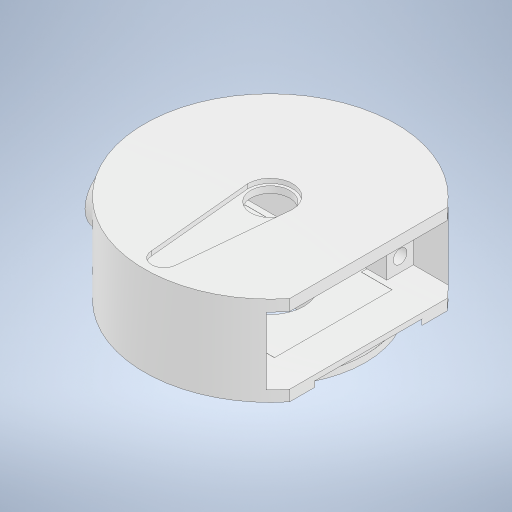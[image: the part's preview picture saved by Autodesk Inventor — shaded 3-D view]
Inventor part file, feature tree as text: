
AUTODESK INVENTOR PART (.ipt)
format: ipt  version: 2023 (Build 270158000, 158)  size: 453,632 bytes
history: mixed  units: in
note: dims shown in document units (in); Inventor stores cm internally (conversion verified against a paired STEP export)
features: extrude x6, sketch x3, projected_geometry x2, delete_face x1, plane x1, move_body x1, imported_body x1
ambient origin geometry x8: Origin, YZ Plane, XZ Plane, XY Plane, X Axis, Y Axis, Z Axis, Center Point
bodies: Solid1 (imported_parasolid), Body1 (imported_parasolid)
feature tree (15):
  sketch  "Skizze1"  dims[d0=0.1417in d1=0.1417in]
  delete_face  "Fläche löschen1"
  plane  "Arbeitsebene1"
  extrude  "Extrusion2"  Depth=0.1417in
  extrude  "Extrusion3"  Depth=0.1417in
  extrude  "Extrusion4"  Depth=0.2362in TaperAngle=0.0deg
  sketch  "Skizze3"  dims[d6=0.3937in d7=0.0in d8=0.2362in d9=0.0in d10=0.1969in d11=0.0in d12=0.3937in d13=0.0in d14=0.3937in d15=0.0in d16=0.3937in d17=0.0in d18=4.1339in d19=0.0in d20=1.9685in]
  extrude  "Extrusion5"  Depth=0.1969in TaperAngle=0.0deg
  extrude  "Extrusion6"  Depth=0.3937in TaperAngle=0.0deg
  extrude  "Extrusion7"  Depth=0.3937in TaperAngle=0.0deg
  move_body  "Move Body1"
  sketch  "Skizze2"  dims[d4=0.1417in d5=0.1417in]
  projected_geometry  "Projizierte Kontur1"
  projected_geometry  "Projizierte Kontur2"
  imported_body  NMx_Import_Brep_tag  [imported B-rep: ~54 faces, bbox_mm=[29.234227, 11.005291, 32.393198]]
